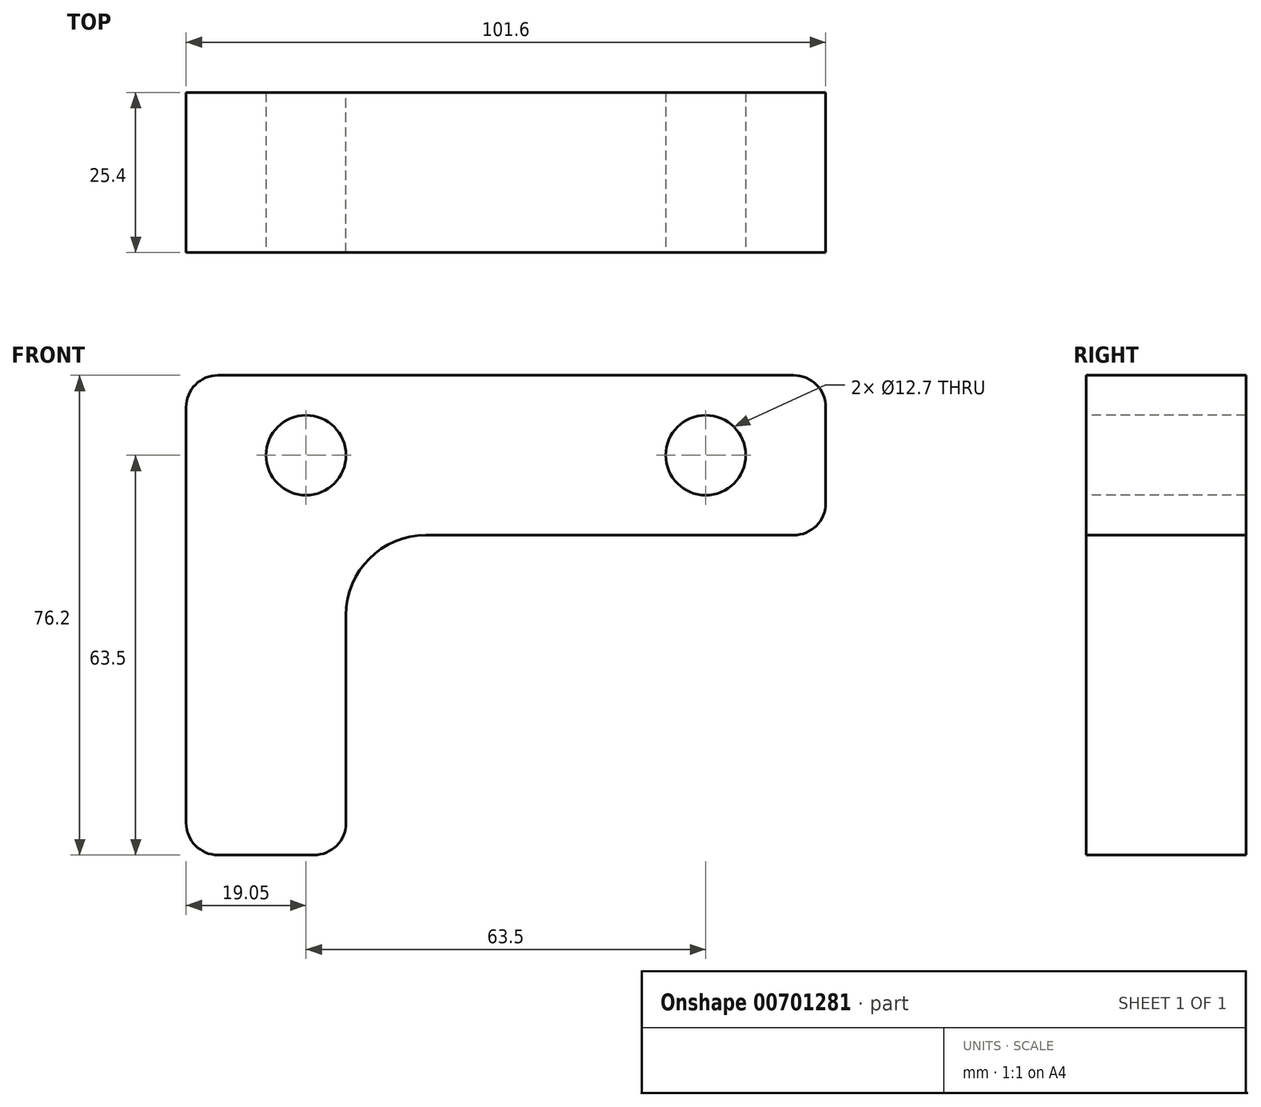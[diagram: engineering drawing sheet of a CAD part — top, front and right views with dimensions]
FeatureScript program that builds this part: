
annotation { "Feature Type Name" : "Feature", "Feature Type Description" : "" }
export const myFeature = defineFeature(function(context is Context, id is Id, definition is map)
    precondition{}
    {
        {
            var Q0;
            Q0=qCreatedBy(makeId("Front.planeOp"),FACE);
            var sketch = newSketch(context, id + "F0", { "sketchPlane" : qUnion([Q0])});
            skLineSegment(sketch, "E0", {"start": v(-50.8, 25.4) * mm, "end": v(-50.8, -50.8) * mm});
            skLineSegment(sketch, "E1", {"start": v(-50.8, -50.8) * mm, "end": v(-25.4, -50.8) * mm});
            skLineSegment(sketch, "E2", {"start": v(-25.4, -50.8) * mm, "end": v(-25.4, -12.7) * mm});
            skLineSegment(sketch, "E3", {"start": v(-12.7, 0) * mm, "end": v(50.8, 0) * mm});
            skLineSegment(sketch, "E4", {"start": v(50.8, 0) * mm, "end": v(50.8, 25.4) * mm});
            skLineSegment(sketch, "E5", {"start": v(50.8, 25.4) * mm, "end": v(-50.8, 25.4) * mm});
            skPoint(sketch, "E6.visualSharp", {"position": v(-25.4, 0) * mm});
            skArc(sketch, "E6.filletArc", {"start": v(-12.7, 0) * mm, "mid": v(-21.68, -3.72) * mm, "end": v(-25.4, -12.7) * mm});
            skSolve(sketch);
        }
        {
            var Q0;
            Q0 = qSketchRegion(id + "F0", true);
            extrude(context, id + "F1", {"entities" : qUnion([Q0]), "endBound" : BoundingType.SYMMETRIC, "depth" : 25.4 * mm, "offsetDistance" : 25.4 * mm});
        }
        {
            var Q0;
            Q0=makeQuery(id+"F1.opExtrude","CAP_FACE",FACE,{"disambiguationData":[OSD([sQuery(id+"F0.wireOp",EDGE,"E0"),sQuery(id+"F0.wireOp",EDGE,"E1"),sQuery(id+"F0.wireOp",EDGE,"E2"),sQuery(id+"F0.wireOp",EDGE,"E3"),sQuery(id+"F0.wireOp",EDGE,"E4"),sQuery(id+"F0.wireOp",EDGE,"E5"),sQuery(id+"F0.wireOp",EDGE,"E6.filletArc")])],"isStart":false});
            var sketch = newSketch(context, id + "F2", { "sketchPlane" : qUnion([Q0])});
            skCircle(sketch, "E7", {"center": v(-31.75, 12.7) * mm, "radius": 6.35 * mm});
            skCircle(sketch, "E8", {"center": v(31.75, 12.7) * mm, "radius": 6.35 * mm});
            skSolve(sketch);
        }
        {
            var Q0;
            Q0 = qSketchRegion(id + "F2", true);
            extrude(context, id + "F3", {"entities" : qUnion([Q0]), "operationType" : NewBodyOperationType.REMOVE, "endBound" : BoundingType.THROUGH_ALL, "oppositeDirection" : true, "depth" : 25.4 * mm, "offsetDistance" : 25.4 * mm});
        }
        {
            var Q0;
            Q0=makeQuery(id+"F1.opExtrude","SWEPT_EDGE",EDGE,{"disambiguationData":[OSD([sQuery(id+"F0.wireOp",EDGE,"E4"),sQuery(id+"F0.wireOp",EDGE,"E5")])]});
            var Q1;
            Q1=makeQuery(id+"F1.opExtrude","SWEPT_EDGE",EDGE,{"disambiguationData":[OSD([sQuery(id+"F0.wireOp",EDGE,"E3"),sQuery(id+"F0.wireOp",EDGE,"E4")])]});
            var Q2;
            Q2=makeQuery(id+"F1.opExtrude","SWEPT_EDGE",EDGE,{"disambiguationData":[OSD([sQuery(id+"F0.wireOp",EDGE,"E1"),sQuery(id+"F0.wireOp",EDGE,"E2")])]});
            var Q3;
            Q3=makeQuery(id+"F1.opExtrude","SWEPT_EDGE",EDGE,{"disambiguationData":[OSD([sQuery(id+"F0.wireOp",EDGE,"E0"),sQuery(id+"F0.wireOp",EDGE,"E5")])]});
            var Q4;
            Q4=makeQuery(id+"F1.opExtrude","SWEPT_EDGE",EDGE,{"disambiguationData":[OSD([sQuery(id+"F0.wireOp",EDGE,"E0"),sQuery(id+"F0.wireOp",EDGE,"E1")])]});
            fillet(context, id + "F4", {"entities" : qUnion([Q0, Q1, Q2, Q3, Q4]), "radius" : 5.08 * mm, "tangentPropagation" : true, "allowEdgeOverflow" : false});
        }
    });
